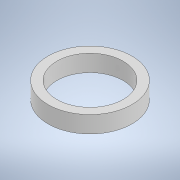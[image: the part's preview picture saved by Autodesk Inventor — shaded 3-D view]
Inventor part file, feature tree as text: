
AUTODESK INVENTOR PART (.ipt)
format: ipt  version: 2020.3 (Build 243373000, 373)  size: 98,816 bytes
history: native  units: mm
features: sketch x1, extrude x1
ambient origin geometry x8: Origin, YZ Plane, XZ Plane, XY Plane, X Axis, Y Axis, Z Axis, Center Point
bodies: Solid1 (feature_tree)
feature tree (2):
  sketch  "Sketch1"  dims[d0=39.5mm d1=50.0mm d2=10.0mm d3=0.0mm]
  extrude  "Extrusion1"  Depth=10.0mm
